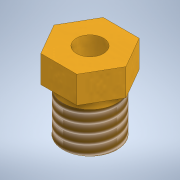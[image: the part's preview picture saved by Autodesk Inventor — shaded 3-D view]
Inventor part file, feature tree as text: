
AUTODESK INVENTOR PART (.ipt)
format: ipt  version: 2020 (Build 240168000, 168)  size: 133,632 bytes
history: native  units: mm
features: sketch x4, extrude x3, thread x1, hole x1
ambient origin geometry x8: Origin, YZ Plane, XZ Plane, XY Plane, X Axis, Y Axis, Z Axis, Center Point
bodies: Solid1 (feature_tree)
feature tree (9):
  extrude  "Extrusion1"  Depth=3.0mm TaperAngle=0.0deg
  extrude  "Extrusion2"  Depth=1.0mm TaperAngle=0.0deg
  extrude  "Extrusion3"  Depth=5.5mm
  thread  "Thread1"  [1 undecoded]
  hole  "Hole1"  [1 undecoded]
  sketch  "Sketch1"  dims[d1=8.0mm d2=3.0mm d3=0.0mm]
  sketch  "Sketch2"  dims[d4=6.0mm d5=1.0mm d6=0.0mm]
  sketch  "Sketch3"  dims[d7=4.5mm d8=0.0mm d9=5.5mm d10=1.0mm]
  sketch  "Sketch4"  dims[d11=3.0mm d12=6.0mm d13=4.0mm d14=2.0mm d15=90.0deg d16=8.0mm d17=20.594885mm d18=0.75mm d19=20.594885mm d20=0.0625mm d21=0.75mm d22=0.375mm]
note: 2 required parameter values undecoded (feature->parameter linkage not recoverable at this tier; creation-order binding heuristic only, values carry confidence <= 0.55)
